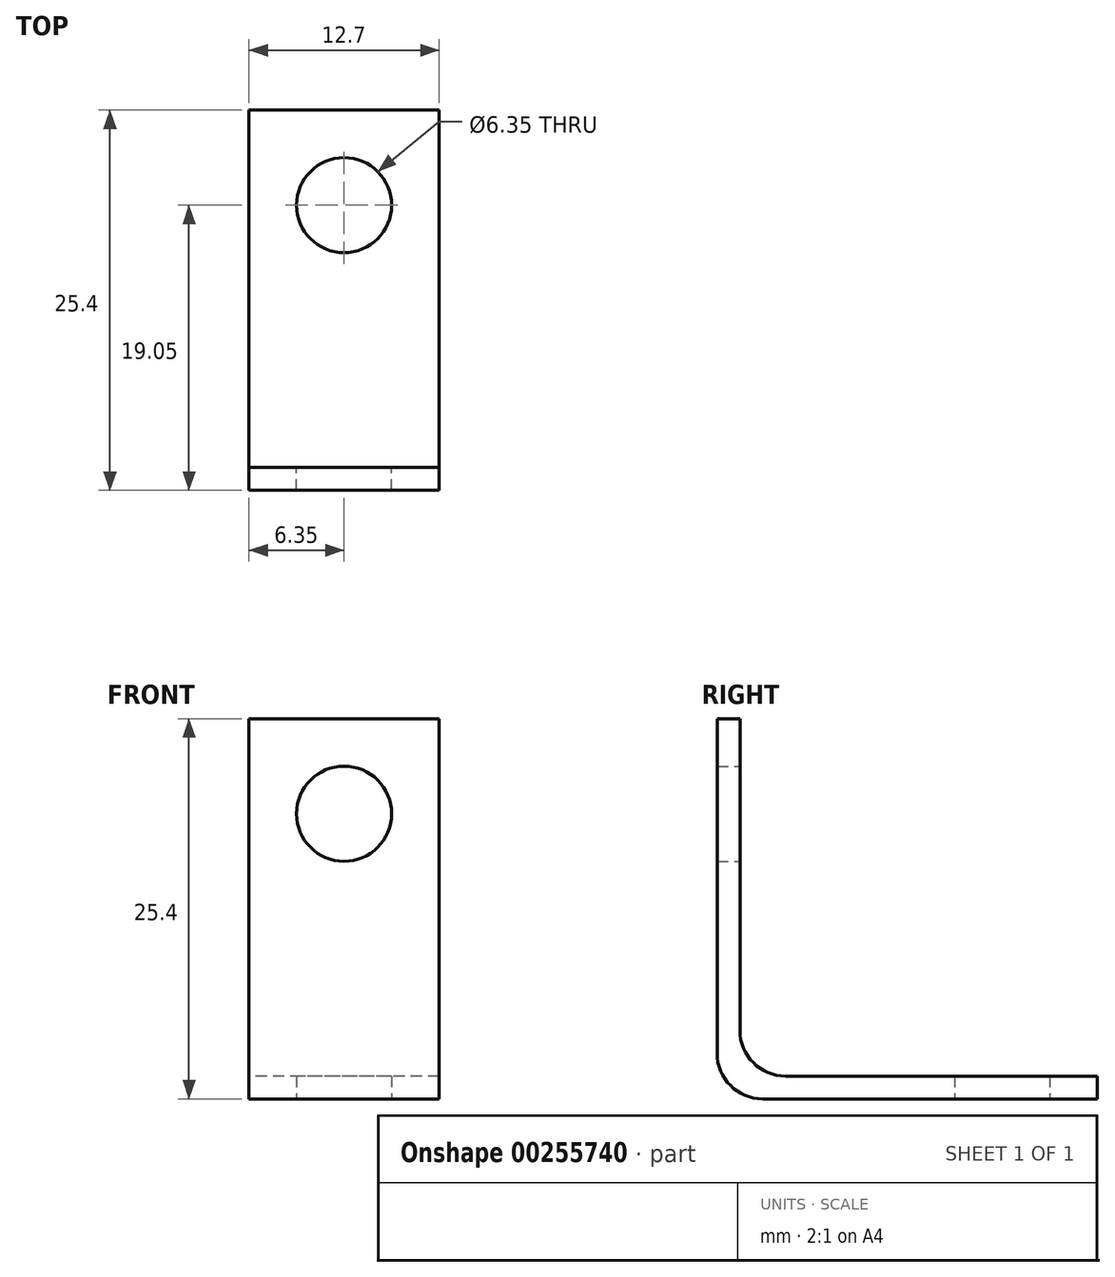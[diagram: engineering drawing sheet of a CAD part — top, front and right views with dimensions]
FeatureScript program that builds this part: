
annotation { "Feature Type Name" : "Feature", "Feature Type Description" : "" }
export const myFeature = defineFeature(function(context is Context, id is Id, definition is map)
    precondition{}
    {
        {
            var Q0;
            Q0=qCreatedBy(makeId("Right.planeOp"),FACE);
            var sketch = newSketch(context, id + "F0", { "sketchPlane" : qUnion([Q0])});
            skLineSegment(sketch, "E0", {"start": v(0, 3.05) * mm, "end": v(0, 25.4) * mm});
            skLineSegment(sketch, "E1", {"start": v(3.05, 0) * mm, "end": v(25.4, 0) * mm});
            skLineSegment(sketch, "E2", {"start": v(0, 25.4) * mm, "end": v(1.52, 25.4) * mm});
            skLineSegment(sketch, "E3", {"start": v(25.4, 0) * mm, "end": v(25.4, 1.52) * mm});
            skLineSegment(sketch, "E4", {"start": v(1.52, 25.4) * mm, "end": v(1.52, 4.57) * mm});
            skLineSegment(sketch, "E5", {"start": v(4.57, 1.52) * mm, "end": v(25.4, 1.52) * mm});
            skPoint(sketch, "E6.visualSharp", {"position": v(1.52, 1.52) * mm});
            skArc(sketch, "E6.filletArc", {"start": v(1.52, 4.57) * mm, "mid": v(2.42, 2.42) * mm, "end": v(4.57, 1.52) * mm});
            skPoint(sketch, "E7.newPointA", {"position": v(0, 0) * mm});
            skPoint(sketch, "E7.newPointB", {"position": v(0, 0) * mm});
            skArc(sketch, "E7.filletArc", {"start": v(0, 3.05) * mm, "mid": v(0.9, 0.9) * mm, "end": v(3.05, 0) * mm});
            skSolve(sketch);
        }
        {
            var Q0;
            {var subQ1=sQuery(id+"F0.wireOp",EDGE,"E1");Q0=makeQuery(id+"F0.imprint","IMPRINT",FACE,{"disambiguationData":[TD([[makeQuery(id+"F0.imprint","IMPRINT",EDGE,{"derivedFrom":subQ1}),1.0]])]});}
            extrude(context, id + "F1", {"entities" : qUnion([Q0]), "depth" : 12.7 * mm});
        }
        {
            var Q0;
            Q0=makeQuery(id+"F1.opExtrude","SWEPT_FACE",FACE,{"disambiguationData":[OSD([sQuery(id+"F0.wireOp",EDGE,"E4")])]});
            var sketch = newSketch(context, id + "F2", { "sketchPlane" : qUnion([Q0])});
            skCircle(sketch, "E8", {"center": v(-6.35, 19.05) * mm, "radius": 3.18 * mm});
            skSolve(sketch);
        }
        {
            var Q0;
            Q0=makeQuery(id+"F2.imprint","IMPRINT",FACE,{"disambiguationData":[TD([[makeQuery(id+"F2.imprint","IMPRINT",EDGE,{"derivedFrom":sQuery(id+"F2.wireOp",EDGE,"E8")}),1.0]])]});
            extrude(context, id + "F3", {"entities" : qUnion([Q0]), "operationType" : NewBodyOperationType.REMOVE, "oppositeDirection" : true, "depth" : 25.4 * mm});
        }
        {
            var Q0;
            Q0=makeQuery(id+"F1.opExtrude","SWEPT_FACE",FACE,{"disambiguationData":[OSD([sQuery(id+"F0.wireOp",EDGE,"E1")])]});
            var sketch = newSketch(context, id + "F4", { "sketchPlane" : qUnion([Q0])});
            skCircle(sketch, "E9", {"center": v(6.35, -19.05) * mm, "radius": 3.18 * mm});
            skSolve(sketch);
        }
        {
            var Q0;
            Q0=makeQuery(id+"F4.imprint","IMPRINT",FACE,{"disambiguationData":[TD([[makeQuery(id+"F4.imprint","IMPRINT",EDGE,{"derivedFrom":sQuery(id+"F4.wireOp",EDGE,"E9")}),1.0]])]});
            extrude(context, id + "F5", {"entities" : qUnion([Q0]), "operationType" : NewBodyOperationType.REMOVE, "oppositeDirection" : true, "depth" : 25.4 * mm});
        }
    });
